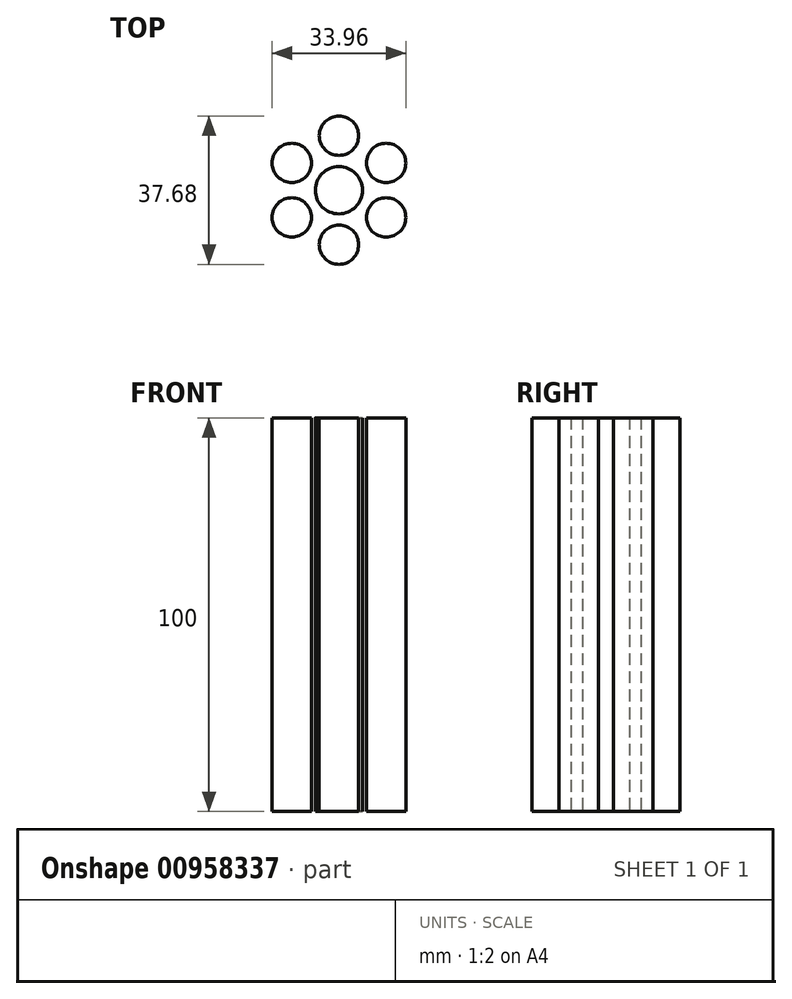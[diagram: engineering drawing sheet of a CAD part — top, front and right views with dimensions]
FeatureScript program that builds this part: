
annotation { "Feature Type Name" : "Feature", "Feature Type Description" : "" }
export const myFeature = defineFeature(function(context is Context, id is Id, definition is map)
    precondition{}
    {
        {
            var Q0;
            Q0=qCreatedBy(makeId("Top.planeOp"),FACE);
            var sketch = newSketch(context, id + "F0", { "sketchPlane" : qUnion([Q0])});
            skCircle(sketch, "E0", {"center": v(0, 0) * mm, "radius": 26.25 * mm});
            skCircle(sketch, "E1", {"center": v(0, 13.84) * mm, "radius": 5 * mm});
            skCircle(sketch, "E2.1.0", {"center": v(-11.98, 6.92) * mm, "radius": 5 * mm});
            skCircle(sketch, "E2.2.0", {"center": v(-11.98, -6.92) * mm, "radius": 5 * mm});
            skCircle(sketch, "E2.3.0", {"center": v(0, -13.84) * mm, "radius": 5 * mm});
            skCircle(sketch, "E2.4.0", {"center": v(11.98, -6.92) * mm, "radius": 5 * mm});
            skCircle(sketch, "E2.5.0", {"center": v(11.98, 6.92) * mm, "radius": 5 * mm});
            skSolve(sketch);
        }
        {
            var Q0;
            Q0=makeQuery(id+"F0.imprint","IMPRINT",FACE,{"disambiguationData":[TD([[makeQuery(id+"F0.imprint","IMPRINT",EDGE,{"derivedFrom":sQuery(id+"F0.wireOp",EDGE,"E0")}),1.0]])]});
            var sketch = newSketch(context, id + "F1", { "sketchPlane" : qUnion([Q0])});
            skCircle(sketch, "E3", {"center": v(0, 0) * mm, "radius": 6 * mm});
            skSolve(sketch);
        }
        {
            var Q0;
            Q0=makeQuery(id+"F0.imprint","IMPRINT",FACE,{"disambiguationData":[TD([[makeQuery(id+"F0.imprint","IMPRINT",EDGE,{"derivedFrom":sQuery(id+"F0.wireOp",EDGE,"E1")}),1.0]])]});
            var Q1;
            Q1=makeQuery(id+"F1.imprint","IMPRINT",FACE,{"disambiguationData":[TD([[makeQuery(id+"F1.imprint","IMPRINT",EDGE,{"derivedFrom":makeQuery(id+"F0.imprint","IMPRINT",EDGE,{"derivedFrom":sQuery(id+"F0.wireOp",EDGE,"E2.4.0")})}),1.0]])]});
            var Q2;
            Q2=makeQuery(id+"F1.imprint","IMPRINT",FACE,{"disambiguationData":[TD([[makeQuery(id+"F1.imprint","IMPRINT",EDGE,{"derivedFrom":makeQuery(id+"F0.imprint","IMPRINT",EDGE,{"derivedFrom":sQuery(id+"F0.wireOp",EDGE,"E2.5.0")})}),1.0]])]});
            var Q3;
            Q3=makeQuery(id+"F0.imprint","IMPRINT",FACE,{"disambiguationData":[TD([[makeQuery(id+"F0.imprint","IMPRINT",EDGE,{"derivedFrom":sQuery(id+"F0.wireOp",EDGE,"E2.1.0")}),1.0]])]});
            var Q4;
            Q4=makeQuery(id+"F1.imprint","IMPRINT",FACE,{"disambiguationData":[TD([[makeQuery(id+"F1.imprint","IMPRINT",EDGE,{"derivedFrom":makeQuery(id+"F0.imprint","IMPRINT",EDGE,{"derivedFrom":sQuery(id+"F0.wireOp",EDGE,"E2.2.0")})}),1.0]])]});
            var Q5;
            Q5=makeQuery(id+"F1.imprint","IMPRINT",FACE,{"disambiguationData":[TD([[makeQuery(id+"F1.imprint","IMPRINT",EDGE,{"derivedFrom":makeQuery(id+"F0.imprint","IMPRINT",EDGE,{"derivedFrom":sQuery(id+"F0.wireOp",EDGE,"E2.3.0")})}),1.0]])]});
            var Q6;
            Q6=makeQuery(id+"F1.imprint","IMPRINT",FACE,{"disambiguationData":[TD([[makeQuery(id+"F1.imprint","IMPRINT",EDGE,{"derivedFrom":sQuery(id+"F1.wireOp",EDGE,"E3")}),1.0]])]});
            extrude(context, id + "F2", {"entities" : qUnion([Q0, Q1, Q2, Q3, Q4, Q5, Q6]), "depth" : 100 * mm, "offsetDistance" : 25 * mm});
        }
    });
